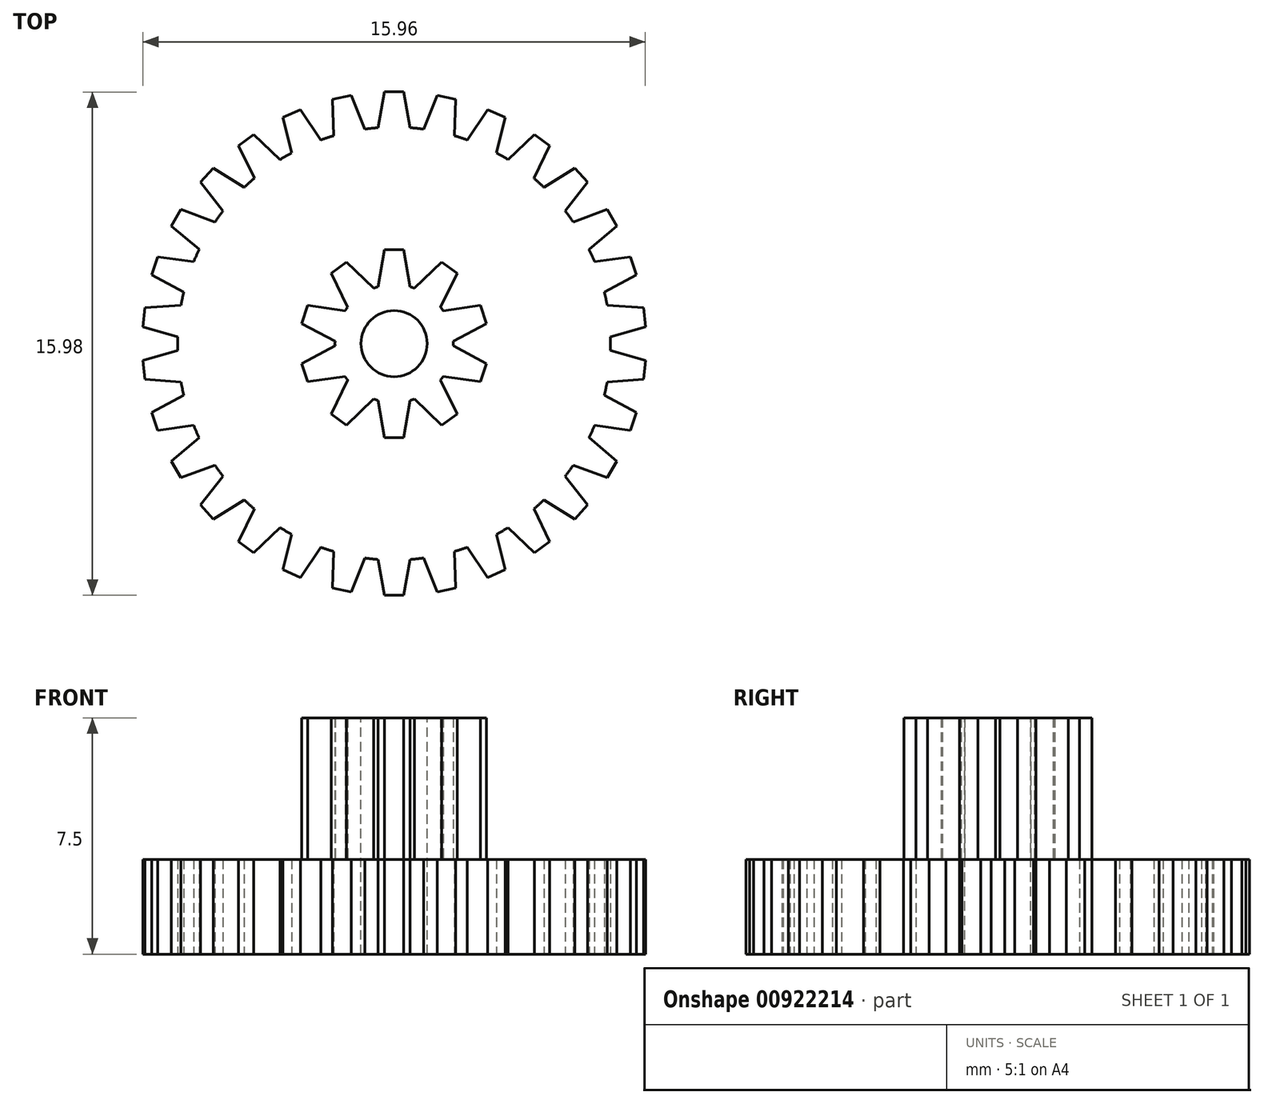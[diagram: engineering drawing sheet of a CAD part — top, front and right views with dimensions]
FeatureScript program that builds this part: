
annotation { "Feature Type Name" : "Feature", "Feature Type Description" : "" }
export const myFeature = defineFeature(function(context is Context, id is Id, definition is map)
    precondition{}
    {
        {
            var Q0;
            Q0=qCreatedBy(makeId("Top.planeOp"),FACE);
            var sketch = newSketch(context, id + "F0", { "sketchPlane" : qUnion([Q0])});
            skCircle(sketch, "E0", {"center": v(0, 0) * mm, "radius": 7.5 * mm, "construction": true});
            skCircle(sketch, "E1", {"center": v(0, 0) * mm, "radius": 8 * mm, "construction": true});
            skCircle(sketch, "E2", {"center": v(0, 0) * mm, "radius": 6.88 * mm});
            skLineSegment(sketch, "E3", {"start": v(0, 6.88) * mm, "end": v(0.5, 6.88) * mm, "construction": true});
            skLineSegment(sketch, "E4", {"start": v(0, 6.88) * mm, "end": v(-0.5, 6.88) * mm, "construction": true});
            skLineSegment(sketch, "E5", {"start": v(-0.5, 6.84) * mm, "end": v(-0.3, 8) * mm, "construction": true});
            skLineSegment(sketch, "E6", {"start": v(0.5, 6.84) * mm, "end": v(0.3, 8) * mm, "construction": true});
            skLineSegment(sketch, "E7", {"start": v(-0.5, 6.85) * mm, "end": v(-0.3, 8) * mm});
            skLineSegment(sketch, "E8", {"start": v(0.3, 8) * mm, "end": v(-0.3, 8) * mm});
            skLineSegment(sketch, "E9", {"start": v(0.3, 8) * mm, "end": v(0.5, 6.86) * mm});
            skLineSegment(sketch, "E10.1.0", {"start": v(-1.92, 6.6) * mm, "end": v(-1.96, 7.76) * mm});
            skLineSegment(sketch, "E10.1.1", {"start": v(-1.37, 7.88) * mm, "end": v(-1.96, 7.76) * mm});
            skLineSegment(sketch, "E10.1.2", {"start": v(-1.37, 7.88) * mm, "end": v(-0.93, 6.81) * mm});
            skLineSegment(sketch, "E10.2.0", {"start": v(-3.25, 6.06) * mm, "end": v(-3.53, 7.18) * mm});
            skLineSegment(sketch, "E10.2.1", {"start": v(-2.98, 7.43) * mm, "end": v(-3.53, 7.18) * mm});
            skLineSegment(sketch, "E10.2.2", {"start": v(-2.98, 7.43) * mm, "end": v(-2.33, 6.47) * mm});
            skLineSegment(sketch, "E11.1.3.0", {"start": v(-4.44, 5.25) * mm, "end": v(-4.94, 6.29) * mm});
            skLineSegment(sketch, "E11.3.3.0", {"start": v(-4.45, 6.65) * mm, "end": v(-4.94, 6.29) * mm});
            skLineSegment(sketch, "E11.6.3.0", {"start": v(-4.45, 6.65) * mm, "end": v(-3.62, 5.84) * mm});
            skLineSegment(sketch, "E11.1.4.0", {"start": v(-5.43, 4.21) * mm, "end": v(-6.14, 5.12) * mm});
            skLineSegment(sketch, "E11.3.4.0", {"start": v(-5.74, 5.57) * mm, "end": v(-6.14, 5.12) * mm});
            skLineSegment(sketch, "E11.6.4.0", {"start": v(-5.74, 5.57) * mm, "end": v(-4.76, 4.96) * mm});
            skLineSegment(sketch, "E11.1.5.0", {"start": v(-6.19, 3) * mm, "end": v(-7.07, 3.74) * mm});
            skLineSegment(sketch, "E11.3.5.0", {"start": v(-6.77, 4.26) * mm, "end": v(-7.07, 3.74) * mm});
            skLineSegment(sketch, "E11.6.5.0", {"start": v(-6.77, 4.26) * mm, "end": v(-5.69, 3.86) * mm});
            skLineSegment(sketch, "E11.1.6.0", {"start": v(-6.67, 1.64) * mm, "end": v(-7.7, 2.18) * mm});
            skLineSegment(sketch, "E11.3.6.0", {"start": v(-7.5, 2.76) * mm, "end": v(-7.7, 2.18) * mm});
            skLineSegment(sketch, "E11.6.6.0", {"start": v(-7.5, 2.76) * mm, "end": v(-6.37, 2.6) * mm});
            skLineSegment(sketch, "E11.1.7.0", {"start": v(-6.87, 0.22) * mm, "end": v(-7.98, 0.53) * mm});
            skLineSegment(sketch, "E11.3.7.0", {"start": v(-7.92, 1.14) * mm, "end": v(-7.98, 0.53) * mm});
            skLineSegment(sketch, "E11.6.7.0", {"start": v(-7.92, 1.14) * mm, "end": v(-6.77, 1.22) * mm});
            skLineSegment(sketch, "E11.1.8.0", {"start": v(-6.76, -1.22) * mm, "end": v(-7.92, -1.14) * mm});
            skLineSegment(sketch, "E11.3.8.0", {"start": v(-7.98, -0.53) * mm, "end": v(-7.92, -1.14) * mm});
            skLineSegment(sketch, "E11.6.8.0", {"start": v(-7.98, -0.53) * mm, "end": v(-6.87, -0.22) * mm});
            skLineSegment(sketch, "E11.1.9.0", {"start": v(-6.36, -2.6) * mm, "end": v(-7.5, -2.76) * mm});
            skLineSegment(sketch, "E11.3.9.0", {"start": v(-7.7, -2.18) * mm, "end": v(-7.5, -2.76) * mm});
            skLineSegment(sketch, "E11.6.9.0", {"start": v(-7.7, -2.18) * mm, "end": v(-6.68, -1.64) * mm});
            skLineSegment(sketch, "E11.1.10.0", {"start": v(-5.68, -3.86) * mm, "end": v(-6.77, -4.26) * mm});
            skLineSegment(sketch, "E11.3.10.0", {"start": v(-7.07, -3.74) * mm, "end": v(-6.77, -4.26) * mm});
            skLineSegment(sketch, "E11.6.10.0", {"start": v(-7.07, -3.74) * mm, "end": v(-6.19, -3) * mm});
            skLineSegment(sketch, "E11.1.11.0", {"start": v(-4.76, -4.96) * mm, "end": v(-5.74, -5.57) * mm});
            skLineSegment(sketch, "E11.3.11.0", {"start": v(-6.14, -5.12) * mm, "end": v(-5.74, -5.57) * mm});
            skLineSegment(sketch, "E11.6.11.0", {"start": v(-6.14, -5.12) * mm, "end": v(-5.43, -4.21) * mm});
            skLineSegment(sketch, "E11.1.12.0", {"start": v(-3.62, -5.84) * mm, "end": v(-4.45, -6.65) * mm});
            skLineSegment(sketch, "E11.3.12.0", {"start": v(-4.94, -6.29) * mm, "end": v(-4.45, -6.65) * mm});
            skLineSegment(sketch, "E11.6.12.0", {"start": v(-4.94, -6.29) * mm, "end": v(-4.44, -5.25) * mm});
            skLineSegment(sketch, "E11.1.13.0", {"start": v(-2.33, -6.47) * mm, "end": v(-2.98, -7.43) * mm});
            skLineSegment(sketch, "E11.3.13.0", {"start": v(-3.53, -7.18) * mm, "end": v(-2.98, -7.43) * mm});
            skLineSegment(sketch, "E11.6.13.0", {"start": v(-3.53, -7.18) * mm, "end": v(-3.25, -6.06) * mm});
            skLineSegment(sketch, "E11.1.14.0", {"start": v(-0.93, -6.8) * mm, "end": v(-1.37, -7.88) * mm});
            skLineSegment(sketch, "E11.3.14.0", {"start": v(-1.96, -7.76) * mm, "end": v(-1.37, -7.88) * mm});
            skLineSegment(sketch, "E11.6.14.0", {"start": v(-1.96, -7.76) * mm, "end": v(-1.92, -6.6) * mm});
            skLineSegment(sketch, "E11.1.15.0", {"start": v(0.5, -6.85) * mm, "end": v(0.3, -8) * mm});
            skLineSegment(sketch, "E11.3.15.0", {"start": v(-0.3, -8) * mm, "end": v(0.3, -8) * mm});
            skLineSegment(sketch, "E11.6.15.0", {"start": v(-0.3, -8) * mm, "end": v(-0.5, -6.86) * mm});
            skLineSegment(sketch, "E11.1.16.0", {"start": v(1.92, -6.6) * mm, "end": v(1.96, -7.76) * mm});
            skLineSegment(sketch, "E11.3.16.0", {"start": v(1.37, -7.88) * mm, "end": v(1.96, -7.76) * mm});
            skLineSegment(sketch, "E11.6.16.0", {"start": v(1.37, -7.88) * mm, "end": v(0.93, -6.81) * mm});
            skLineSegment(sketch, "E11.1.17.0", {"start": v(3.25, -6.06) * mm, "end": v(3.53, -7.18) * mm});
            skLineSegment(sketch, "E11.3.17.0", {"start": v(2.98, -7.43) * mm, "end": v(3.53, -7.18) * mm});
            skLineSegment(sketch, "E11.6.17.0", {"start": v(2.98, -7.43) * mm, "end": v(2.33, -6.47) * mm});
            skLineSegment(sketch, "E11.1.18.0", {"start": v(4.44, -5.25) * mm, "end": v(4.94, -6.29) * mm});
            skLineSegment(sketch, "E11.3.18.0", {"start": v(4.45, -6.65) * mm, "end": v(4.94, -6.29) * mm});
            skLineSegment(sketch, "E11.6.18.0", {"start": v(4.45, -6.65) * mm, "end": v(3.62, -5.84) * mm});
            skLineSegment(sketch, "E11.1.19.0", {"start": v(5.43, -4.21) * mm, "end": v(6.14, -5.12) * mm});
            skLineSegment(sketch, "E11.3.19.0", {"start": v(5.74, -5.57) * mm, "end": v(6.14, -5.12) * mm});
            skLineSegment(sketch, "E11.6.19.0", {"start": v(5.74, -5.57) * mm, "end": v(4.76, -4.96) * mm});
            skLineSegment(sketch, "E11.1.20.0", {"start": v(6.19, -3) * mm, "end": v(7.07, -3.74) * mm});
            skLineSegment(sketch, "E11.3.20.0", {"start": v(6.77, -4.26) * mm, "end": v(7.07, -3.74) * mm});
            skLineSegment(sketch, "E11.6.20.0", {"start": v(6.77, -4.26) * mm, "end": v(5.69, -3.86) * mm});
            skLineSegment(sketch, "E11.1.21.0", {"start": v(6.67, -1.64) * mm, "end": v(7.7, -2.18) * mm});
            skLineSegment(sketch, "E11.3.21.0", {"start": v(7.5, -2.76) * mm, "end": v(7.7, -2.18) * mm});
            skLineSegment(sketch, "E11.6.21.0", {"start": v(7.5, -2.76) * mm, "end": v(6.37, -2.6) * mm});
            skLineSegment(sketch, "E11.1.22.0", {"start": v(6.87, -0.22) * mm, "end": v(7.98, -0.53) * mm});
            skLineSegment(sketch, "E11.3.22.0", {"start": v(7.92, -1.14) * mm, "end": v(7.98, -0.53) * mm});
            skLineSegment(sketch, "E11.6.22.0", {"start": v(7.92, -1.14) * mm, "end": v(6.77, -1.22) * mm});
            skLineSegment(sketch, "E11.1.23.0", {"start": v(6.76, 1.22) * mm, "end": v(7.92, 1.14) * mm});
            skLineSegment(sketch, "E11.3.23.0", {"start": v(7.98, 0.53) * mm, "end": v(7.92, 1.14) * mm});
            skLineSegment(sketch, "E11.6.23.0", {"start": v(7.98, 0.53) * mm, "end": v(6.87, 0.22) * mm});
            skLineSegment(sketch, "E11.1.24.0", {"start": v(6.36, 2.6) * mm, "end": v(7.5, 2.76) * mm});
            skLineSegment(sketch, "E11.3.24.0", {"start": v(7.7, 2.18) * mm, "end": v(7.5, 2.76) * mm});
            skLineSegment(sketch, "E11.6.24.0", {"start": v(7.7, 2.18) * mm, "end": v(6.68, 1.64) * mm});
            skLineSegment(sketch, "E11.1.25.0", {"start": v(5.68, 3.86) * mm, "end": v(6.77, 4.26) * mm});
            skLineSegment(sketch, "E11.3.25.0", {"start": v(7.07, 3.74) * mm, "end": v(6.77, 4.26) * mm});
            skLineSegment(sketch, "E11.6.25.0", {"start": v(7.07, 3.74) * mm, "end": v(6.19, 3) * mm});
            skLineSegment(sketch, "E11.1.26.0", {"start": v(4.76, 4.96) * mm, "end": v(5.74, 5.57) * mm});
            skLineSegment(sketch, "E11.3.26.0", {"start": v(6.14, 5.12) * mm, "end": v(5.74, 5.57) * mm});
            skLineSegment(sketch, "E11.6.26.0", {"start": v(6.14, 5.12) * mm, "end": v(5.43, 4.21) * mm});
            skLineSegment(sketch, "E11.1.27.0", {"start": v(3.62, 5.84) * mm, "end": v(4.45, 6.65) * mm});
            skLineSegment(sketch, "E11.3.27.0", {"start": v(4.94, 6.29) * mm, "end": v(4.45, 6.65) * mm});
            skLineSegment(sketch, "E11.6.27.0", {"start": v(4.94, 6.29) * mm, "end": v(4.44, 5.25) * mm});
            skLineSegment(sketch, "E11.1.28.0", {"start": v(2.33, 6.47) * mm, "end": v(2.98, 7.43) * mm});
            skLineSegment(sketch, "E11.3.28.0", {"start": v(3.53, 7.18) * mm, "end": v(2.98, 7.43) * mm});
            skLineSegment(sketch, "E11.6.28.0", {"start": v(3.53, 7.18) * mm, "end": v(3.25, 6.06) * mm});
            skLineSegment(sketch, "E11.1.29.0", {"start": v(0.93, 6.8) * mm, "end": v(1.37, 7.88) * mm});
            skLineSegment(sketch, "E11.3.29.0", {"start": v(1.96, 7.76) * mm, "end": v(1.37, 7.88) * mm});
            skLineSegment(sketch, "E11.6.29.0", {"start": v(1.96, 7.76) * mm, "end": v(1.92, 6.6) * mm});
            skSolve(sketch);
        }
        {
            var Q0;
            Q0 = qSketchRegion(id + "F0", true);
            extrude(context, id + "F1", {"entities" : qUnion([Q0]), "depth" : 3 * mm, "offsetDistance" : 25 * mm});
        }
        {
            var Q0;
            Q0=makeQuery(id+"F1.opExtrude","CAP_FACE",FACE,{"disambiguationData":[OSD([sQuery(id+"F0.wireOp",EDGE,"E2"),sQuery(id+"F0.wireOp",EDGE,"E7"),sQuery(id+"F0.wireOp",EDGE,"E8"),sQuery(id+"F0.wireOp",EDGE,"E9"),sQuery(id+"F0.wireOp",EDGE,"E10.1.0"),sQuery(id+"F0.wireOp",EDGE,"E10.1.1"),sQuery(id+"F0.wireOp",EDGE,"E10.1.2"),sQuery(id+"F0.wireOp",EDGE,"E10.2.0"),sQuery(id+"F0.wireOp",EDGE,"E10.2.1"),sQuery(id+"F0.wireOp",EDGE,"E10.2.2"),sQuery(id+"F0.wireOp",EDGE,"E11.1.3.0"),sQuery(id+"F0.wireOp",EDGE,"E11.3.3.0"),sQuery(id+"F0.wireOp",EDGE,"E11.6.3.0"),sQuery(id+"F0.wireOp",EDGE,"E11.1.4.0"),sQuery(id+"F0.wireOp",EDGE,"E11.3.4.0"),sQuery(id+"F0.wireOp",EDGE,"E11.6.4.0"),sQuery(id+"F0.wireOp",EDGE,"E11.1.5.0"),sQuery(id+"F0.wireOp",EDGE,"E11.3.5.0"),sQuery(id+"F0.wireOp",EDGE,"E11.6.5.0"),sQuery(id+"F0.wireOp",EDGE,"E11.1.6.0"),sQuery(id+"F0.wireOp",EDGE,"E11.3.6.0"),sQuery(id+"F0.wireOp",EDGE,"E11.6.6.0"),sQuery(id+"F0.wireOp",EDGE,"E11.1.7.0"),sQuery(id+"F0.wireOp",EDGE,"E11.3.7.0"),sQuery(id+"F0.wireOp",EDGE,"E11.6.7.0"),sQuery(id+"F0.wireOp",EDGE,"E11.1.8.0"),sQuery(id+"F0.wireOp",EDGE,"E11.3.8.0"),sQuery(id+"F0.wireOp",EDGE,"E11.6.8.0"),sQuery(id+"F0.wireOp",EDGE,"E11.1.9.0"),sQuery(id+"F0.wireOp",EDGE,"E11.3.9.0"),sQuery(id+"F0.wireOp",EDGE,"E11.6.9.0"),sQuery(id+"F0.wireOp",EDGE,"E11.1.10.0"),sQuery(id+"F0.wireOp",EDGE,"E11.3.10.0"),sQuery(id+"F0.wireOp",EDGE,"E11.6.10.0"),sQuery(id+"F0.wireOp",EDGE,"E11.1.11.0"),sQuery(id+"F0.wireOp",EDGE,"E11.3.11.0"),sQuery(id+"F0.wireOp",EDGE,"E11.6.11.0"),sQuery(id+"F0.wireOp",EDGE,"E11.1.12.0"),sQuery(id+"F0.wireOp",EDGE,"E11.3.12.0"),sQuery(id+"F0.wireOp",EDGE,"E11.6.12.0"),sQuery(id+"F0.wireOp",EDGE,"E11.1.13.0"),sQuery(id+"F0.wireOp",EDGE,"E11.3.13.0"),sQuery(id+"F0.wireOp",EDGE,"E11.6.13.0"),sQuery(id+"F0.wireOp",EDGE,"E11.1.14.0"),sQuery(id+"F0.wireOp",EDGE,"E11.3.14.0"),sQuery(id+"F0.wireOp",EDGE,"E11.6.14.0"),sQuery(id+"F0.wireOp",EDGE,"E11.1.15.0"),sQuery(id+"F0.wireOp",EDGE,"E11.3.15.0"),sQuery(id+"F0.wireOp",EDGE,"E11.6.15.0"),sQuery(id+"F0.wireOp",EDGE,"E11.1.16.0"),sQuery(id+"F0.wireOp",EDGE,"E11.3.16.0"),sQuery(id+"F0.wireOp",EDGE,"E11.6.16.0"),sQuery(id+"F0.wireOp",EDGE,"E11.1.17.0"),sQuery(id+"F0.wireOp",EDGE,"E11.3.17.0"),sQuery(id+"F0.wireOp",EDGE,"E11.6.17.0"),sQuery(id+"F0.wireOp",EDGE,"E11.1.18.0"),sQuery(id+"F0.wireOp",EDGE,"E11.3.18.0"),sQuery(id+"F0.wireOp",EDGE,"E11.6.18.0"),sQuery(id+"F0.wireOp",EDGE,"E11.1.19.0"),sQuery(id+"F0.wireOp",EDGE,"E11.3.19.0"),sQuery(id+"F0.wireOp",EDGE,"E11.6.19.0"),sQuery(id+"F0.wireOp",EDGE,"E11.1.20.0"),sQuery(id+"F0.wireOp",EDGE,"E11.3.20.0"),sQuery(id+"F0.wireOp",EDGE,"E11.6.20.0"),sQuery(id+"F0.wireOp",EDGE,"E11.1.21.0"),sQuery(id+"F0.wireOp",EDGE,"E11.3.21.0"),sQuery(id+"F0.wireOp",EDGE,"E11.6.21.0"),sQuery(id+"F0.wireOp",EDGE,"E11.1.22.0"),sQuery(id+"F0.wireOp",EDGE,"E11.3.22.0"),sQuery(id+"F0.wireOp",EDGE,"E11.6.22.0"),sQuery(id+"F0.wireOp",EDGE,"E11.1.23.0"),sQuery(id+"F0.wireOp",EDGE,"E11.3.23.0"),sQuery(id+"F0.wireOp",EDGE,"E11.6.23.0"),sQuery(id+"F0.wireOp",EDGE,"E11.1.24.0"),sQuery(id+"F0.wireOp",EDGE,"E11.3.24.0"),sQuery(id+"F0.wireOp",EDGE,"E11.6.24.0"),sQuery(id+"F0.wireOp",EDGE,"E11.1.25.0"),sQuery(id+"F0.wireOp",EDGE,"E11.3.25.0"),sQuery(id+"F0.wireOp",EDGE,"E11.6.25.0"),sQuery(id+"F0.wireOp",EDGE,"E11.1.26.0"),sQuery(id+"F0.wireOp",EDGE,"E11.3.26.0"),sQuery(id+"F0.wireOp",EDGE,"E11.6.26.0"),sQuery(id+"F0.wireOp",EDGE,"E11.1.27.0"),sQuery(id+"F0.wireOp",EDGE,"E11.3.27.0"),sQuery(id+"F0.wireOp",EDGE,"E11.6.27.0"),sQuery(id+"F0.wireOp",EDGE,"E11.1.28.0"),sQuery(id+"F0.wireOp",EDGE,"E11.3.28.0"),sQuery(id+"F0.wireOp",EDGE,"E11.6.28.0"),sQuery(id+"F0.wireOp",EDGE,"E11.1.29.0"),sQuery(id+"F0.wireOp",EDGE,"E11.3.29.0"),sQuery(id+"F0.wireOp",EDGE,"E11.6.29.0")])],"isStart":false});
            var sketch = newSketch(context, id + "F2", { "sketchPlane" : qUnion([Q0])});
            skCircle(sketch, "E12", {"center": v(0, 0) * mm, "radius": 2.5 * mm, "construction": true});
            skCircle(sketch, "E13", {"center": v(0, 0) * mm, "radius": 3 * mm, "construction": true});
            skCircle(sketch, "E14", {"center": v(0, 0) * mm, "radius": 1.88 * mm});
            skLineSegment(sketch, "E15", {"start": v(0, 1.88) * mm, "end": v(0.5, 1.88) * mm, "construction": true});
            skLineSegment(sketch, "E16", {"start": v(0, 1.88) * mm, "end": v(-0.5, 1.88) * mm, "construction": true});
            skLineSegment(sketch, "E17", {"start": v(-0.51, 1.8) * mm, "end": v(-0.3, 2.98) * mm, "construction": true});
            skLineSegment(sketch, "E18", {"start": v(0.51, 1.8) * mm, "end": v(0.3, 2.98) * mm, "construction": true});
            skLineSegment(sketch, "E19", {"start": v(-0.51, 1.8) * mm, "end": v(-0.3, 2.98) * mm});
            skLineSegment(sketch, "E20", {"start": v(0.3, 2.98) * mm, "end": v(-0.3, 2.98) * mm});
            skLineSegment(sketch, "E21", {"start": v(0.3, 2.98) * mm, "end": v(0.51, 1.8) * mm});
            skLineSegment(sketch, "E22.1.0", {"start": v(-1.47, 1.16) * mm, "end": v(-2, 2.24) * mm});
            skLineSegment(sketch, "E22.1.1", {"start": v(-1.5, 2.6) * mm, "end": v(-2, 2.24) * mm});
            skLineSegment(sketch, "E22.1.2", {"start": v(-1.5, 2.6) * mm, "end": v(-0.65, 1.76) * mm});
            skLineSegment(sketch, "E22.2.0", {"start": v(-1.87, 0.07) * mm, "end": v(-2.93, 0.63) * mm});
            skLineSegment(sketch, "E22.2.1", {"start": v(-2.74, 1.21) * mm, "end": v(-2.93, 0.63) * mm});
            skLineSegment(sketch, "E22.2.2", {"start": v(-2.74, 1.21) * mm, "end": v(-1.56, 1.04) * mm});
            skLineSegment(sketch, "E23.1.3.0", {"start": v(-1.56, -1.04) * mm, "end": v(-2.74, -1.21) * mm});
            skLineSegment(sketch, "E23.3.3.0", {"start": v(-2.93, -0.63) * mm, "end": v(-2.74, -1.21) * mm});
            skLineSegment(sketch, "E23.6.3.0", {"start": v(-2.93, -0.63) * mm, "end": v(-1.87, -0.07) * mm});
            skLineSegment(sketch, "E23.1.4.0", {"start": v(-0.65, -1.76) * mm, "end": v(-1.5, -2.6) * mm});
            skLineSegment(sketch, "E23.3.4.0", {"start": v(-2, -2.24) * mm, "end": v(-1.5, -2.6) * mm});
            skLineSegment(sketch, "E23.6.4.0", {"start": v(-2, -2.24) * mm, "end": v(-1.47, -1.16) * mm});
            skLineSegment(sketch, "E23.1.5.0", {"start": v(0.51, -1.8) * mm, "end": v(0.3, -2.98) * mm});
            skLineSegment(sketch, "E23.3.5.0", {"start": v(-0.3, -2.98) * mm, "end": v(0.3, -2.98) * mm});
            skLineSegment(sketch, "E23.6.5.0", {"start": v(-0.3, -2.98) * mm, "end": v(-0.51, -1.8) * mm});
            skLineSegment(sketch, "E23.1.6.0", {"start": v(1.47, -1.16) * mm, "end": v(2, -2.24) * mm});
            skLineSegment(sketch, "E23.3.6.0", {"start": v(1.5, -2.6) * mm, "end": v(2, -2.24) * mm});
            skLineSegment(sketch, "E23.6.6.0", {"start": v(1.5, -2.6) * mm, "end": v(0.65, -1.76) * mm});
            skLineSegment(sketch, "E23.1.7.0", {"start": v(1.87, -0.07) * mm, "end": v(2.93, -0.63) * mm});
            skLineSegment(sketch, "E23.3.7.0", {"start": v(2.74, -1.21) * mm, "end": v(2.93, -0.63) * mm});
            skLineSegment(sketch, "E23.6.7.0", {"start": v(2.74, -1.21) * mm, "end": v(1.56, -1.04) * mm});
            skLineSegment(sketch, "E23.1.8.0", {"start": v(1.56, 1.04) * mm, "end": v(2.74, 1.21) * mm});
            skLineSegment(sketch, "E23.3.8.0", {"start": v(2.93, 0.63) * mm, "end": v(2.74, 1.21) * mm});
            skLineSegment(sketch, "E23.6.8.0", {"start": v(2.93, 0.63) * mm, "end": v(1.87, 0.07) * mm});
            skLineSegment(sketch, "E23.1.9.0", {"start": v(0.65, 1.76) * mm, "end": v(1.5, 2.6) * mm});
            skLineSegment(sketch, "E23.3.9.0", {"start": v(2, 2.24) * mm, "end": v(1.5, 2.6) * mm});
            skLineSegment(sketch, "E23.6.9.0", {"start": v(2, 2.24) * mm, "end": v(1.47, 1.16) * mm});
            skSolve(sketch);
        }
        {
            var Q0;
            Q0 = qSketchRegion(id + "F2", true);
            extrude(context, id + "F3", {"entities" : qUnion([Q0]), "operationType" : NewBodyOperationType.ADD, "depth" : 4.5 * mm, "offsetDistance" : 25 * mm});
        }
        {
            var Q0;
            Q0=makeQuery(id+"F3.opExtrude","CAP_FACE",FACE,{"disambiguationData":[OSD([sQuery(id+"F2.wireOp",EDGE,"E14"),sQuery(id+"F2.wireOp",EDGE,"E19"),sQuery(id+"F2.wireOp",EDGE,"E20"),sQuery(id+"F2.wireOp",EDGE,"E21"),sQuery(id+"F2.wireOp",EDGE,"E22.1.0"),sQuery(id+"F2.wireOp",EDGE,"E22.1.1"),sQuery(id+"F2.wireOp",EDGE,"E22.1.2"),sQuery(id+"F2.wireOp",EDGE,"E22.2.0"),sQuery(id+"F2.wireOp",EDGE,"E22.2.1"),sQuery(id+"F2.wireOp",EDGE,"E22.2.2"),sQuery(id+"F2.wireOp",EDGE,"E23.1.3.0"),sQuery(id+"F2.wireOp",EDGE,"E23.3.3.0"),sQuery(id+"F2.wireOp",EDGE,"E23.6.3.0"),sQuery(id+"F2.wireOp",EDGE,"E23.1.4.0"),sQuery(id+"F2.wireOp",EDGE,"E23.3.4.0"),sQuery(id+"F2.wireOp",EDGE,"E23.6.4.0"),sQuery(id+"F2.wireOp",EDGE,"E23.1.5.0"),sQuery(id+"F2.wireOp",EDGE,"E23.3.5.0"),sQuery(id+"F2.wireOp",EDGE,"E23.6.5.0"),sQuery(id+"F2.wireOp",EDGE,"E23.1.6.0"),sQuery(id+"F2.wireOp",EDGE,"E23.3.6.0"),sQuery(id+"F2.wireOp",EDGE,"E23.6.6.0"),sQuery(id+"F2.wireOp",EDGE,"E23.1.7.0"),sQuery(id+"F2.wireOp",EDGE,"E23.3.7.0"),sQuery(id+"F2.wireOp",EDGE,"E23.6.7.0"),sQuery(id+"F2.wireOp",EDGE,"E23.1.8.0"),sQuery(id+"F2.wireOp",EDGE,"E23.3.8.0"),sQuery(id+"F2.wireOp",EDGE,"E23.6.8.0"),sQuery(id+"F2.wireOp",EDGE,"E23.1.9.0"),sQuery(id+"F2.wireOp",EDGE,"E23.3.9.0"),sQuery(id+"F2.wireOp",EDGE,"E23.6.9.0")])],"isStart":false});
            var sketch = newSketch(context, id + "F4", { "sketchPlane" : qUnion([Q0])});
            skCircle(sketch, "E24", {"center": v(0, 0) * mm, "radius": 1.05 * mm});
            skSolve(sketch);
        }
        {
            var Q0;
            Q0 = qSketchRegion(id + "F4", true);
            extrude(context, id + "F5", {"entities" : qUnion([Q0]), "operationType" : NewBodyOperationType.REMOVE, "endBound" : BoundingType.THROUGH_ALL, "oppositeDirection" : true, "depth" : 25 * mm, "offsetDistance" : 25 * mm});
        }
    });
